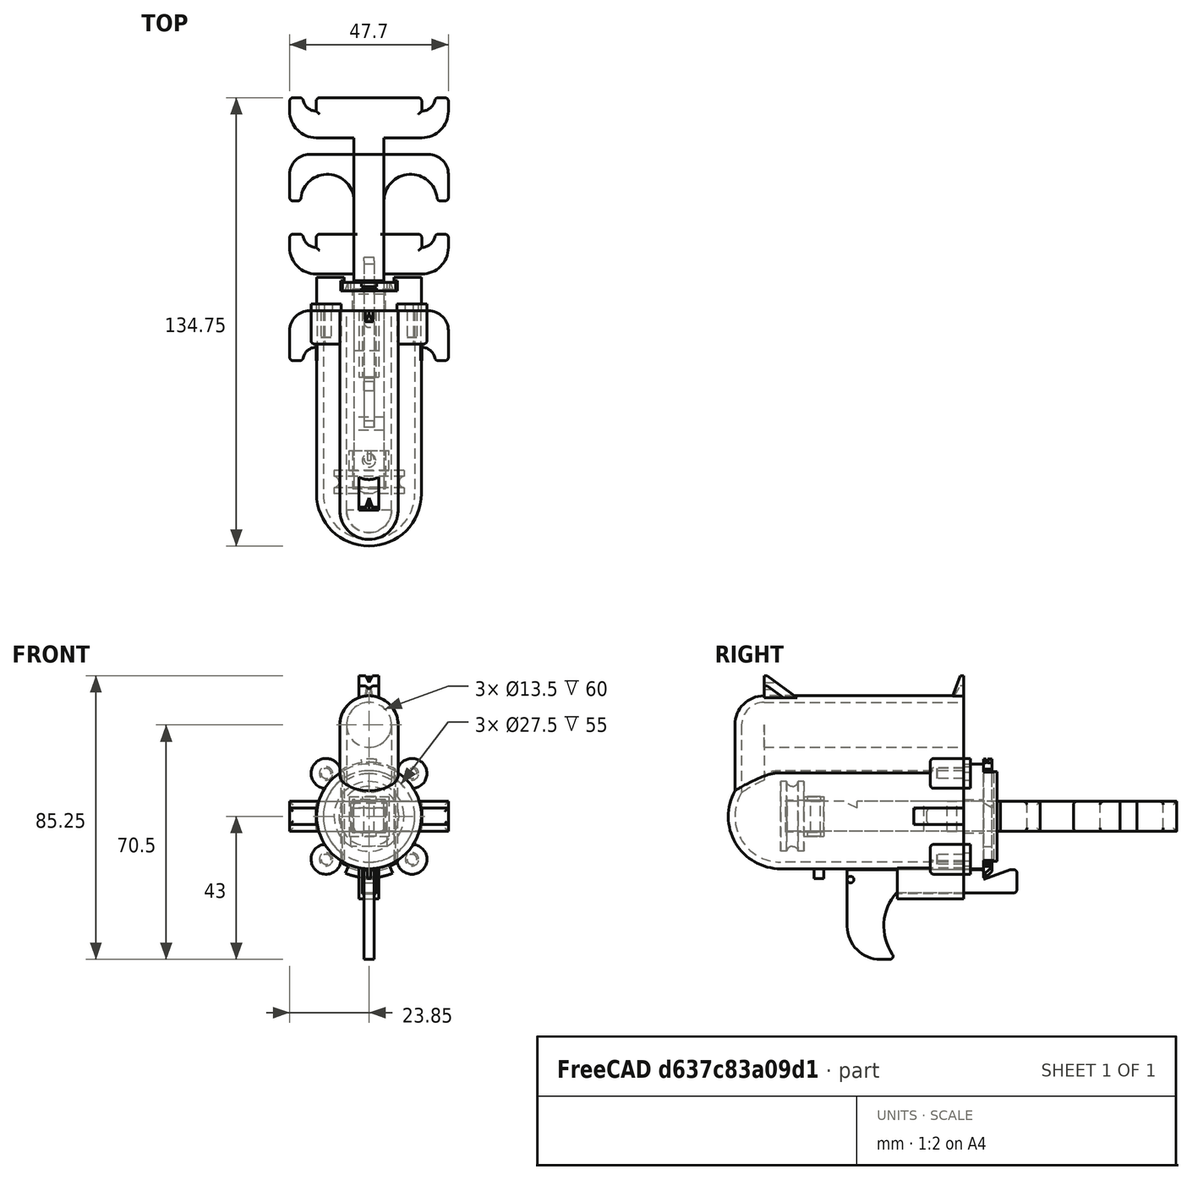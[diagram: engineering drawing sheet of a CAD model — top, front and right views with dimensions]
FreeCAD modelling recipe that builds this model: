
FCSTD DOCUMENT  (FreeCAD 0.19R24267 +99 (Git))
Label: miniU
License: All rights reserved
LicenseURL: http://en.wikipedia.org/wiki/All_rights_reserved
objects: PartDesign::SubtractiveCylinder×25, PartDesign::AdditiveCylinder×21, PartDesign::AdditiveBox×18, PartDesign::Fillet×15, PartDesign::Mirrored×10, PartDesign::Body×10, PartDesign::AdditiveSphere×8, PartDesign::PolarPattern×8, PartDesign::SubtractiveBox×8, PartDesign::SubtractiveSphere×6, PartDesign::SubtractiveWedge×5, PartDesign::AdditiveWedge×5, Sketcher::SketchObject×1, PartDesign::SubtractiveTorus×1, PartDesign::Chamfer×1
note: 255 computed .brp shape members not serialized (recipe doc carries the construction recipe); baked Part::Feature solids carry a one-line shape summary decoded from their .brp

FEATURE [PartDesign::AdditiveCylinder] Cylinder001  label="dart_holder_body"
  Angle = 360
  AttacherType = Attacher::AttachEngine3D
  AttachmentOffset = pos=(0,27.5,0) rot=(0,0,1;0rad)
  Height = 60
  MapMode = 5
  Placement = pos=(0,-6.1e-15,27.5) rot=(1,0,0;1.5708rad)
  Radius = 8.75
  Support = -> [XZ_Plane]
  expr: .AttachmentOffset.Base.y = Sketch.Constraints.chamberToHolder
  expr: Radius = Sketch.Constraints.rDartHolderOutside
  expr: Height = Sketch.Constraints.bodyLength + Sketch.Constraints.holderOffset
FEATURE [PartDesign::AdditiveBox] Box  label="chamber_holder_connector"
  AttacherType = Attacher::AttachEngine3D
  AttachmentOffset = pos=(-8.75,0,-60) rot=(0,0,1;0rad)
  BaseFeature = -> Cylinder001
  Height = 60
  Length = 17.5
  MapMode = 5
  Placement = pos=(-8.75,-60,27.5) rot=(-1,0,0;1.5708rad)
  Support = -> [Cylinder001]
  Width = 27.5
  expr: Length = Cylinder001.Radius * 2
  expr: .AttachmentOffset.Base.x = -Cylinder001.Radius
  expr: .AttachmentOffset.Base.z = -Cylinder001.Height
  expr: Height = Cylinder001.Height
  expr: Width = Sketch.Constraints.chamberToHolder
FEATURE [PartDesign::AdditiveSphere] Sphere  label="chamber_butt"
  Angle1 = -90
  Angle2 = 90
  Angle3 = 180
  AttacherType = Attacher::AttachEngine3D
  AttachmentOffset = pos=(-8.75,5,0) rot=(0,0,-1;3.14159rad)
  BaseFeature = -> Box
  MapMode = 5
  Placement = pos=(0,-55,-1.31e-14) rot=(-1,0,0;3.14159rad)
  Radius = 15.75
  Support = -> [Box]
  expr: .AttachmentOffset.Base.y = Sketch.Constraints.holderOffset
  expr: .AttachmentOffset.Base.x = -Cylinder001.Radius
  expr: Radius = Sketch.Constraints.rAirChamberOutside
FEATURE [PartDesign::AdditiveSphere] Sphere002  label="holder_butt"
  Angle1 = -90
  Angle2 = 90
  Angle3 = 360
  AttacherType = Attacher::AttachEngine3D
  BaseFeature = -> Sphere
  MapMode = 11
  Placement = pos=(0,-60,27.5) rot=(0.57735,-0.57735,0.57735;2.0944rad)
  Radius = 8.75
  Support = -> [Cylinder001]
  expr: Radius = Cylinder001.Radius
FEATURE [PartDesign::AdditiveCylinder] Cylinder  label="butt_connector"
  Angle = 180
  AttacherType = Attacher::AttachEngine3D
  AttachmentOffset = pos=(-8.75,0,-27.5) rot=(0,0,1;3.14159rad)
  BaseFeature = -> Sphere002
  Height = 27.5
  MapMode = 5
  Placement = pos=(0,-60,27.5) rot=(1,0,0;3.14159rad)
  Radius = 8.75
  Support = -> [Box]
  expr: .AttachmentOffset.Base.x = -Radius
  expr: Radius = Sphere002.Radius
  expr: Height = Box.Width
  expr: .AttachmentOffset.Base.z = -Box.Width
FEATURE [Sketcher::SketchObject] Sketch
  FullyConstrained = false
  MapMode = 5
  Placement = pos=(0,0,0) rot=(1,0,0;1.5708rad)
  expr: .Constraints.rAirChamber = 13.75mm
  expr: .Constraints.rDartHolderOutside = .Constraints.rDartHolder + .Constraints.wallThickness
  expr: .Constraints.chamberToHolder = .Constraints.rAirChamberOutside + .Constraints.rDartHolderOutside + .Constraints.triggerClearance
  expr: .Constraints.plungerHeadSpace = .Constraints.plungerHeadHeight + .Constraints.plungerConnectorHeight + 7mm
  sketch-geometry (40):
    g0: Circle CenterX=0 CenterY=0 CenterZ=0 NormalX=0 NormalY=0 NormalZ=1 AngleXU=0 Radius=13.75
    g1: Circle CenterX=0 CenterY=0 CenterZ=0 NormalX=0 NormalY=0 NormalZ=1 AngleXU=0 Radius=15.75
    g2: LineSegment StartX=0 StartY=0 StartZ=0 EndX=-11.1369 EndY=11.1369 EndZ=0
    g3: LineSegment StartX=0 StartY=0 StartZ=0 EndX=11.1369 EndY=-11.1369 EndZ=0
    g4: LineSegment StartX=0 StartY=0 StartZ=0 EndX=-11.1369 EndY=-11.1369 EndZ=0
    g5: LineSegment StartX=0 StartY=0 StartZ=0 EndX=11.1369 EndY=11.1369 EndZ=0
    g6: Circle CenterX=-12.9047 CenterY=12.9047 CenterZ=0 NormalX=0 NormalY=0 NormalZ=1 AngleXU=0 Radius=4.5
    g7: Circle CenterX=-12.9047 CenterY=12.9047 CenterZ=0 NormalX=0 NormalY=0 NormalZ=1 AngleXU=0 Radius=1.5
    g8: Circle CenterX=12.9047 CenterY=12.9047 CenterZ=0 NormalX=0 NormalY=0 NormalZ=1 AngleXU=0 Radius=4.5
    g9: Circle CenterX=12.9047 CenterY=-12.9047 CenterZ=0 NormalX=0 NormalY=0 NormalZ=1 AngleXU=0 Radius=4.5
    g10: Circle CenterX=-12.9047 CenterY=-12.9047 CenterZ=0 NormalX=0 NormalY=0 NormalZ=1 AngleXU=0 Radius=4.5
    g11: Circle CenterX=12.9047 CenterY=12.9047 CenterZ=0 NormalX=0 NormalY=0 NormalZ=1 AngleXU=0 Radius=2.5
    g12: Circle CenterX=12.9047 CenterY=-12.9047 CenterZ=0 NormalX=0 NormalY=0 NormalZ=1 AngleXU=0 Radius=2.5
    g13: Circle CenterX=-12.9047 CenterY=-12.9047 CenterZ=0 NormalX=0 NormalY=0 NormalZ=1 AngleXU=0 Radius=2.5
    g14: LineSegment StartX=-64.4343 StartY=16.9456 StartZ=0 EndX=-65.991 EndY=15.6899 EndZ=0
    g15: Circle CenterX=0 CenterY=27.5 CenterZ=0 NormalX=0 NormalY=0 NormalZ=1 AngleXU=0 Radius=6.75
    g16: Circle CenterX=0 CenterY=27.5 CenterZ=0 NormalX=0 NormalY=0 NormalZ=1 AngleXU=0 Radius=8.75
    g17: LineSegment StartX=-40.3343 StartY=20.9092 StartZ=0 EndX=-43.3342 EndY=20.8833 EndZ=0
    g18: LineSegment StartX=-25.2142 StartY=68.5251 StartZ=0 EndX=-61.5111 EndY=27.2028 EndZ=0
    g19: LineSegment StartX=21.11 StartY=51.0184 StartZ=0 EndX=24.006 EndY=46.9425 EndZ=0
    g20: LineSegment StartX=-12.7279 StartY=-12.7279 StartZ=0 EndX=12.7279 EndY=-12.7279 EndZ=0
    g21: LineSegment StartX=52.0801 StartY=33.9087 StartZ=0 EndX=59.1988 EndY=26.8856 EndZ=0
    g22: LineSegment StartX=35.6743 StartY=43.6176 StartZ=0 EndX=37.6673 EndY=43.4507 EndZ=0
    g23: Circle CenterX=-12.9047 CenterY=12.9047 CenterZ=0 NormalX=0 NormalY=0 NormalZ=1 AngleXU=0 Radius=2
    g24: LineSegment StartX=-26.9818 StartY=14.1414 StartZ=0 EndX=-26.9818 EndY=4.14137 EndZ=0
    g25: LineSegment StartX=-27.1419 StartY=18.6048 StartZ=0 EndX=-17.1419 EndY=18.6048 EndZ=0
    g26: LineSegment StartX=97.724 StartY=55.6573 StartZ=0 EndX=98.9263 EndY=52.9088 EndZ=0
    g27: LineSegment StartX=114.207 StartY=50.7764 StartZ=0 EndX=114.698 EndY=50.6847 EndZ=0
    g28: LineSegment StartX=128.072 StartY=57.8158 StartZ=0 EndX=130.022 EndY=55.5362 EndZ=0
    g29: LineSegment StartX=-62.4879 StartY=52.9152 StartZ=0 EndX=-78.8492 EndY=39.7505 EndZ=0
    g30: LineSegment StartX=-15.7414 StartY=69.7309 StartZ=0 EndX=44.2586 EndY=69.7309 EndZ=0
    g31: Circle CenterX=50.0754 CenterY=-16.528 CenterZ=0 NormalX=0 NormalY=0 NormalZ=1 AngleXU=0 Radius=9.625
    g32: LineSegment StartX=83.804 StartY=28.6893 StartZ=0 EndX=88.0476 EndY=23.1224 EndZ=0
    g33: LineSegment StartX=90.4529 StartY=40.1785 StartZ=0 EndX=95.8588 EndY=35.7314 EndZ=0
    g34: Circle CenterX=93.0757 CenterY=-11.2423 CenterZ=0 NormalX=0 NormalY=0 NormalZ=1 AngleXU=0 Radius=9.25
    g35: Circle CenterX=102.66 CenterY=-16.1107 CenterZ=0 NormalX=0 NormalY=0 NormalZ=1 AngleXU=0 Radius=1.5
    g36: LineSegment StartX=-47.4906 StartY=-5.12483 StartZ=0 EndX=-47.4906 EndY=-8.12483 EndZ=0
    g37: LineSegment StartX=-47.4906 StartY=-8.12483 StartZ=0 EndX=-40.4906 EndY=-8.12483 EndZ=0
    g38: LineSegment StartX=-97.7001 StartY=1.7101 StartZ=0 EndX=-97.7001 EndY=-14.2899 EndZ=0
    g39: LineSegment StartX=-37.3838 StartY=-26.4694 StartZ=0 EndX=-35.296 EndY=-32.0944 EndZ=0
  constraints (78):
    c: Coincident(g0,g-1)
    c: Coincident(g1,g0)
    c: Radius(g0) = 13.75  'rAirChamber'
    c: Radius(g1) = 15.75  'rAirChamberOutside'
    c: Coincident(g2,g0)
    c: PointOnObject(g2,g1)
    c: Coincident(g3,g0)
    c: PointOnObject(g3,g1)
    c: Coincident(g4,g0)
    c: PointOnObject(g4,g1)
    c: Angle(g2) = 2.35619
    c: Angle(g3) = -0.785398
    c: Angle(g4) = -2.35619
    c: Coincident(g5,g0)
    c: PointOnObject(g5,g1)
    c: Angle(g5) = 0.785398
    c: PointOnObject(g6,g2)
    c: Diameter(g6) = 9  'dNutOutside'
    c: Coincident(g7,g6)
    c: Diameter(g7) = 3  'dInsert'
    c: Equal(g8,g10)
    c: PointOnObject(g8,g5)
    c: PointOnObject(g9,g3)
    c: PointOnObject(g10,g4)
    c: Coincident(g11,g8)
    c: Coincident(g12,g9)
    c: Coincident(g13,g10)
    c: Equal(g11,g12)
    c: Distance(g14) = 2  'wallThickness'
    c: PointOnObject(g15,g-2)
    c: Coincident(g16,g15)
    c: Radius(g15) = 6.75  'rDartHolder'
    c: Radius(g16) = 8.75  'rDartHolderOutside'
    c: Distance(g15,g0) = 27.5  'chamberToHolder'
    c: Distance(g17) = 3  'triggerClearance'
    c: Distance(g18) = 55  'bodyLength'
    c: Tangent(g6,g0)
    c: Tangent(g8,g0)
    c: Tangent(g9,g0)
    c: Tangent(g10,g0)
    c: Distance(g19) = 5  'holderOffset'
    c: Distance(g20) = 25.4558  'threadDistance'
    c: Distance(g21) = 10  'chamberCapThickness'
    c: Radius(g6) = 4.5  'rNutOutside'
    c: Radius(g7) = 1.5  'rInsert'
    c: Distance(g22) = 2  'capThreadThickness'
    c: Coincident(g23,g6)
    c: Radius(g23) = 2  'rThread'
    c: Vertical(g24)
    c: Horizontal(g25)
    c: Distance(g25) = 10  'capHoleWidth'
    c: Distance(g24) = 10  'capHoleLength'
    c: Equal(g6,g8)
    c: Equal(g8,g9)
    c: Equal(g12,g13)
    c: Distance(g26) = 3  'triggerFrame'
    c: Distance(g27) = 0.5  'triggerFrameClearance'
    c: Distance(g28) = 3  'triggerFrameThickness'
    c: Distance(g29) = 21  'plungerHeadSpace'
    c: Horizontal(g30)
    c: Distance(g30) = 60  'plungerLength'
    c: Diameter(g31) = 19.25  'dPlungerHead'
    c: Radius(g31) = 9.625  'rPlungerHead'
    c: Distance(g32) = 7  'plungerHeadHeight'
    c: Distance(g33) = 7  'plungerConnectorHeight'
    c: Tangent(g35,g34)
    c: Diameter(g34) = 18.5  'oRingD1'
    c: Diameter(g35) = 3  'oRingD2'
    c: Radius(g34) = 9.25  'oRingR1'
    c: Radius(g35) = 1.5  'oRingR2'
    c: Vertical(g36)
    c: Coincident(g37,g36)
    c: Horizontal(g37)
    c: Distance(g36) = 3  'triggerPullerWidth'
    c: Distance(g37) = 7  'triggerPullerLength'
    c: Vertical(g38)
    c: Distance(g38) = 16  'pullerSpacing'
    c: Distance(g39) = 6  'sightHeight'
FEATURE [PartDesign::AdditiveCylinder] Cylinder002  label="air_chamber_body"
  Angle = 360
  AttacherType = Attacher::AttachEngine3D
  BaseFeature = -> Cylinder
  Height = 55
  MapMode = 2
  Placement = pos=(0,0,0) rot=(1,0,0;1.5708rad)
  Radius = 15.75
  Support = -> [Sketch]
  expr: Radius = Sketch.Constraints.rAirChamberOutside
  expr: Height = Sketch.Constraints.bodyLength
FEATURE [PartDesign::SubtractiveCylinder] Cylinder003  label="air_chamber"
  Angle = 360
  AttacherType = Attacher::AttachEngine3D
  BaseFeature = -> Cylinder002
  Height = 55
  MapMode = 2
  Placement = pos=(0,0,0) rot=(1,0,0;1.5708rad)
  Radius = 13.75
  Support = -> [Sketch]
  expr: Radius = Sketch.Constraints.rAirChamber
  expr: Height = Cylinder001.Height - Sketch.Constraints.holderOffset
FEATURE [PartDesign::SubtractiveCylinder] Cylinder004  label="butt_connector_channel"
  Angle = 180
  AttacherType = Attacher::AttachEngine3D
  BaseFeature = -> Cylinder003
  Height = 27.5
  MapMode = 2
  Placement = pos=(0,-60,27.5) rot=(1,0,0;3.14159rad)
  Radius = 6.75
  Support = -> [Cylinder]
  expr: Radius = Cylinder.Radius - 2mm
  expr: Height = Cylinder.Height
FEATURE [PartDesign::SubtractiveSphere] Sphere003
  Angle1 = -90
  Angle2 = 90
  Angle3 = 180
  AttacherType = Attacher::AttachEngine3D
  BaseFeature = -> Cylinder004
  MapMode = 2
  Placement = pos=(0,-55,-1.31e-14) rot=(1,0,0;3.14159rad)
  Radius = 13.75
  Support = -> [Sphere]
  expr: Radius = Sketch.Constraints.rAirChamber
FEATURE [PartDesign::SubtractiveCylinder] Cylinder005  label="dart_holder"
  Angle = 360
  AttacherType = Attacher::AttachEngine3D
  AttachmentOffset = pos=(0,0,-60) rot=(0,0,1;0rad)
  BaseFeature = -> Sphere003
  Height = 60
  MapMode = 5
  Placement = pos=(0,-60,27.5) rot=(-1,0,0;1.5708rad)
  Radius = 6.75
  Support = -> [Cylinder001]
  expr: Radius = Cylinder001.Radius - 2mm
  expr: Height = Cylinder001.Height
  expr: .AttachmentOffset.Base.z = -Cylinder001.Height
FEATURE [PartDesign::SubtractiveSphere] Sphere004
  Angle1 = -90
  Angle2 = 90
  Angle3 = 360
  AttacherType = Attacher::AttachEngine3D
  BaseFeature = -> Cylinder005
  MapMode = 2
  Placement = pos=(0,-60,27.5) rot=(-0.57735,0.57735,-0.57735;4.18879rad)
  Radius = 6.75
  Support = -> [Sphere002]
  expr: Radius = Sphere002.Radius - 2mm
FEATURE [PartDesign::AdditiveCylinder] Cylinder006
  Angle = 360
  AttacherType = Attacher::AttachEngine3D
  BaseFeature = -> Sphere004
  Height = 10
  MapMode = 11
  Placement = pos=(-12.9047,2.9e-15,12.9047) rot=(0.57735,-0.57735,0.57735;2.0944rad)
  Radius = 4.5
  Support = -> [Sketch]
  expr: Radius = Sketch.Constraints.dNutOutside / 2
FEATURE [PartDesign::PolarPattern] PolarPattern
  Angle = 360
  Axis = -> Y_Axis
  BaseFeature = -> Cylinder006
  Occurrences = 4
  Originals = -> [Cylinder006]
  Placement = pos=(-12.9047,3e-15,12.9047) rot=(0.57735,-0.57735,0.57735;2.0944rad)
FEATURE [PartDesign::SubtractiveCylinder] Cylinder007
  Angle = 360
  AttacherType = Attacher::AttachEngine3D
  BaseFeature = -> PolarPattern
  Height = 8
  MapMode = 11
  Placement = pos=(-12.9047,2.9e-15,12.9047) rot=(0.57735,-0.57735,0.57735;2.0944rad)
  Radius = 1.5
  Support = -> [Sketch]
  expr: Radius = Sketch.Constraints.dInsert / 2
  expr: Height = Cylinder006.Height - 2mm
FEATURE [PartDesign::AdditiveCylinder] Cylinder008  label="cap_body"
  Angle = 360
  AttacherType = Attacher::AttachEngine3D
  AttachmentOffset = pos=(0,0,0) rot=(0,1,0;3.14159rad)
  Height = 10
  MapMode = 5
  Placement = pos=(0,0,0) rot=(0,0.707107,0.707107;3.14159rad)
  Radius = 15.75
  Refine = true
  Support = -> [XZ_Plane001]
  expr: Radius = Sketch.Constraints.rAirChamberOutside
  expr: Height = Sketch.Constraints.chamberCapThickness
FEATURE [PartDesign::AdditiveCylinder] Cylinder009
  Angle = 360
  AttacherType = Attacher::AttachEngine3D
  AttachmentOffset = pos=(0,0,0) rot=(0,1,0;3.14159rad)
  BaseFeature = -> Cylinder008
  Height = 2
  MapMode = 11
  Placement = pos=(12.9047,-2.9e-15,-12.9047) rot=(-0.57735,0.57735,0.57735;2.0944rad)
  Radius = 4.5
  Refine = true
  Support = -> [Sketch]
  expr: Height = Sketch.Constraints.capThreadThickness
  expr: Radius = Sketch.Constraints.rNutOutside
FEATURE [PartDesign::PolarPattern] PolarPattern002
  Angle = 360
  Axis = -> Y_Axis001
  BaseFeature = -> Cylinder009
  Occurrences = 4
  Originals = -> [Cylinder009]
  Placement = pos=(12.9047,-3e-15,-12.9047) rot=(0.57735,-0.57735,-0.57735;4.18879rad)
  Refine = true
FEATURE [PartDesign::SubtractiveCylinder] Cylinder010
  Angle = 360
  AttacherType = Attacher::AttachEngine3D
  AttachmentOffset = pos=(0,0,0) rot=(0,1,0;3.14159rad)
  BaseFeature = -> PolarPattern002
  Height = 2
  MapMode = 11
  Placement = pos=(12.9047,2.9e-15,12.9047) rot=(-0.57735,0.57735,0.57735;2.0944rad)
  Radius = 2
  Refine = true
  Support = -> [Sketch]
  expr: Radius = Sketch.Constraints.rThread
  expr: Height = Cylinder009.Height
FEATURE [PartDesign::PolarPattern] PolarPattern003
  Angle = 360
  Axis = -> Y_Axis001
  BaseFeature = -> Cylinder010
  Occurrences = 4
  Originals = -> [Cylinder010]
  Placement = pos=(12.9047,3e-15,12.9047) rot=(0.57735,-0.57735,-0.57735;4.18879rad)
  Refine = true
FEATURE [PartDesign::PolarPattern] PolarPattern001
  Angle = 360
  Axis = -> Y_Axis
  BaseFeature = -> Cylinder007
  Occurrences = 4
  Originals = -> [Cylinder007]
  Placement = pos=(-12.9047,3e-15,12.9047) rot=(0.57735,-0.57735,0.57735;2.0944rad)
FEATURE [PartDesign::SubtractiveBox] Box001  label="cap_hole"
  AttacherType = Attacher::AttachEngine3D
  AttachmentOffset = pos=(5,-5,0) rot=(0,1,0;3.14159rad)
  BaseFeature = -> PolarPattern003
  Height = 10
  Length = 10
  MapMode = 5
  Placement = pos=(5,1.1e-15,-5) rot=(0,0.707107,0.707107;3.14159rad)
  Refine = true
  Support = -> [XZ_Plane001]
  Width = 10
  expr: Height = Cylinder008.Height
  expr: Width = Sketch.Constraints.capHoleWidth
  expr: Length = Sketch.Constraints.capHoleLength
  expr: .AttachmentOffset.Base.y = -Width / 2
  expr: .AttachmentOffset.Base.x = Length / 2
FEATURE [PartDesign::AdditiveBox] Box002  label="plungerBody"
  AttacherType = Attacher::AttachEngine3D
  AttachmentOffset = pos=(-4.5,-4.5,0) rot=(0,0,1;0rad)
  Height = 64
  Length = 9
  MapMode = 5
  Placement = pos=(-4.5,1e-15,-4.5) rot=(1,0,0;1.5708rad)
  Refine = true
  Support = -> [XZ_Plane003]
  Width = 9
  expr: .AttachmentOffset.Base.x = -Length / 2
  expr: .AttachmentOffset.Base.y = -Width / 2
  expr: Length = Sketch.Constraints.capHoleLength - 1mm
  expr: Width = Sketch.Constraints.capHoleWidth - 1mm
  expr: Height = Sketch.Constraints.bodyLength + 9mm
FEATURE [PartDesign::SubtractiveWedge] Wedge
  AttacherType = Attacher::AttachEngine3D
  AttachmentOffset = pos=(-9,43,-2) rot=(0,0,1;0rad)
  BaseFeature = -> Box002
  MapMode = 5
  Placement = pos=(4.5,-43,2.5) rot=(0,0,1;3.14159rad)
  Refine = true
  Support = -> [Box002]
  X2max = 9
  X2min = 0
  Xmax = 9
  Xmin = 0
  Ymax = 4
  Ymin = 0
  Z2max = 2
  Z2min = 2
  Zmax = 2
  Zmin = 0
  expr: X2max = Xmax
  expr: Xmax = <<plungerBody>>.Length
  expr: .AttachmentOffset.Base.y = Box002.Height - Sketch.Constraints.plungerHeadSpace
  expr: .AttachmentOffset.Base.x = -Xmax / 2 - Box002.Length / 2
FEATURE [PartDesign::SubtractiveBox] Box003  label="trigger_housing"
  AttacherType = Attacher::AttachEngine3D
  AttachmentOffset = pos=(16.25,-8.5,-1) rot=(0,1,0;3.14159rad)
  BaseFeature = -> Box001
  Height = 3.1
  Length = 32.5
  MapMode = 11
  Placement = pos=(-8.5,9,16.25) rot=(0.57735,0.57735,-0.57735;2.0944rad)
  Refine = true
  Support = -> [Box001]
  Width = 17
  expr: .AttachmentOffset.Base.z = -Sketch.Constraints.wallThickness / 2
  expr: Height = Sketch.Constraints.triggerFrameThickness + 0.1mm
  expr: Width = Box001.Length + Sketch.Constraints.triggerFrame * 2 + Sketch.Constraints.triggerFrameClearance * 2
  expr: Length = Cylinder008.Radius * 2 + 1mm
  expr: .AttachmentOffset.Base.y = -Width / 2
  expr: .AttachmentOffset.Base.x = Length / 2
FEATURE [PartDesign::SubtractiveBox] Box004  label="cap_cutout"
  AttacherType = Attacher::AttachEngine3D
  AttachmentOffset = pos=(16.25,-7.5,0) rot=(0,1,0;3.14159rad)
  BaseFeature = -> Box003
  Height = 1
  Length = 32.5
  MapMode = 11
  Placement = pos=(-7.5,10,16.25) rot=(-0.57735,-0.57735,0.57735;4.18879rad)
  Refine = true
  Support = -> [Box003]
  Width = 15
  expr: Height = Sketch.Constraints.wallThickness / 2
  expr: Width = <<trigger_housing>>.Width - 2mm
  expr: .AttachmentOffset.Base.y = -Width / 2
  expr: .AttachmentOffset.Base.x = Length / 2
  expr: Length = <<trigger_housing>>.Length
FEATURE [PartDesign::AdditiveCylinder] Cylinder013
  Angle = 15
  AttacherType = Attacher::AttachEngine3D
  AttachmentOffset = pos=(0,0,2.5) rot=(0.659346,0.75184,0;3.14159rad)
  Height = 2.5
  MapMode = 5
  Placement = pos=(0,-2.5,-6e-16) rot=(0.527011,0.600941,0.600941;4.11164rad)
  Radius = 17.25
  Refine = true
  Support = -> [XZ_Plane002]
  expr: Radius = Cylinder008.Radius + 1.5mm
  expr: .AttachmentOffset.Rotation.Yaw = 90° + Angle / 2
  expr: .AttachmentOffset.Base.z = Sketch.Constraints.triggerFrameThickness - 0.5mm
FEATURE [PartDesign::SubtractiveBox] Box007
  AttacherType = Attacher::AttachEngine3D
  AttachmentOffset = pos=(0,3,1) rot=(1,0,0;3.14159rad)
  BaseFeature = -> Cylinder013
  Height = 3
  Length = 0.5
  MapMode = 45
  Placement = pos=(-3,-1.25,18.2008) rot=(0.707107,0.707107,0;3.14159rad)
  Refine = true
  Support = -> [Cylinder013]
  Width = 6
FEATURE [PartDesign::AdditiveCylinder] Cylinder011
  Angle = 360
  AttacherType = Attacher::AttachEngine3D
  BaseFeature = -> Box007
  Height = 2.5
  MapMode = 2
  Placement = pos=(0,0,0) rot=(1,0,0;1.5708rad)
  Radius = 16.25
  Refine = true
  Support = -> [XZ_Plane002]
  expr: Height = Sketch.Constraints.triggerFrameThickness - 0.5mm
  expr: Radius = Cylinder008.Radius + 0.5mm
FEATURE [PartDesign::AdditiveCylinder] Cylinder012
  Angle = 45
  AttacherType = Attacher::AttachEngine3D
  AttachmentOffset = pos=(0,0,0) rot=(0,0,-1;1.96349rad)
  BaseFeature = -> Cylinder011
  Height = 2.5
  MapMode = 5
  Placement = pos=(0,0,0) rot=(0.427192,0.639338,-0.639338;2.33414rad)
  Radius = 18.5
  Refine = true
  Support = -> [XZ_Plane002]
  expr: Height = Cylinder011.Height
  expr: .AttachmentOffset.Rotation.Yaw = -90deg - Angle / 2
FEATURE [PartDesign::SubtractiveCylinder] Cylinder014
  Angle = 360
  AttacherType = Attacher::AttachEngine3D
  AttachmentOffset = pos=(0,0,0) rot=(1,0,0;3.14159rad)
  BaseFeature = -> Cylinder012
  Height = 10
  MapMode = 5
  Placement = pos=(0,0,0) rot=(1,0,0;4.71239rad)
  Radius = 16.25
  Refine = true
  Support = -> [XZ_Plane002]
  expr: Radius = <<air_chamber_body>>.Radius + 0.5mm
FEATURE [PartDesign::SubtractiveBox] Box005
  AttacherType = Attacher::AttachEngine3D
  AttachmentOffset = pos=(-5.5,-9,0) rot=(0,0,1;0rad)
  BaseFeature = -> Cylinder014
  Height = 2.5
  Length = 11
  MapMode = 5
  Placement = pos=(-5.5,2e-15,-9) rot=(1,0,0;1.5708rad)
  Refine = true
  Support = -> [XZ_Plane002]
  Width = 14
  expr: Length = <<cap_hole>>.Length + 1mm
  expr: .AttachmentOffset.Base.x = -Length / 2
  expr: Width = <<cap_hole>>.Width + 4mm
  expr: .AttachmentOffset.Base.y = -Width / 2 - 2mm
  expr: Height = Cylinder011.Height
FEATURE [PartDesign::AdditiveWedge] Wedge001
  AttacherType = Attacher::AttachEngine3D
  AttachmentOffset = pos=(11,3,0) rot=(0,0,1;3.14159rad)
  BaseFeature = -> Box005
  MapMode = 5
  Placement = pos=(5.5,-3,5) rot=(0,-1,0;3.14159rad)
  Refine = true
  Support = -> [Box005]
  X2max = 11
  X2min = 0
  Xmax = 11
  Xmin = 0
  Ymax = 3
  Ymin = 0.5
  Z2max = 1
  Z2min = 0
  Zmax = 2.5
  Zmin = 0
  expr: X2max = Box005.Length
  expr: Xmax = Box005.Length
FEATURE [PartDesign::SubtractiveBox] Box006
  AttacherType = Attacher::AttachEngine3D
  AttachmentOffset = pos=(8,-16.25,0) rot=(0,0,1;0rad)
  BaseFeature = -> Wedge001
  Height = 10
  Length = 11
  MapMode = 5
  Placement = pos=(8,3.6e-15,-16.25) rot=(1,0,0;1.5708rad)
  Refine = true
  Support = -> [XZ_Plane002]
  Width = 32.5
  expr: Width = Cylinder011.Radius * 2
  expr: .AttachmentOffset.Base.y = -Width / 2
  expr: .AttachmentOffset.Base.x = <<trigger_housing>>.Width / 2 - 0.5mm
FEATURE [PartDesign::Mirrored] Mirrored
  BaseFeature = -> Box006
  MirrorPlane = -> YZ_Plane002
  Originals = -> [Box006]
  Placement = pos=(8,4e-15,-16.25) rot=(1,0,0;1.5708rad)
  Refine = true
FEATURE [PartDesign::Fillet] Fillet005
  Base = -> Box004 [Edge16,Edge8,Edge2,Edge10]
  BaseFeature = -> Box004
  Placement = pos=(-7.5,10,16.25) rot=(0.57735,0.57735,-0.57735;2.0944rad)
  Radius = 0.5
  Refine = true
  SupportTransform = false
FEATURE [PartDesign::Body] Body001  label="cap"
  Group = -> [Cylinder008,Cylinder009,PolarPattern002,Cylinder010,PolarPattern003,Box001,Box003,Box004,Fillet005]
  Origin = -> Origin001
  Tip = -> Fillet005
FEATURE [PartDesign::AdditiveCylinder] Cylinder019  label="oRingHolder"
  Angle = 360
  AttacherType = Attacher::AttachEngine3D
  Height = 7
  MapMode = 5
  Placement = pos=(0,0,0) rot=(1,0,0;1.5708rad)
  Radius = 10.5
  Refine = true
  Support = -> [XZ_Plane004]
  expr: Radius = Sketch.Constraints.oRingR1 + Sketch.Constraints.oRingR2 - 0.25mm
  expr: Height = Sketch.Constraints.plungerHeadHeight
FEATURE [PartDesign::AdditiveBox] Box016  label="plungerConnector"
  AttacherType = Attacher::AttachEngine3D
  AttachmentOffset = pos=(-6,-6,0) rot=(0,0,1;0rad)
  BaseFeature = -> Cylinder019
  Height = 6
  Length = 12
  MapMode = 5
  Placement = pos=(-6,-1.3e-15,6) rot=(-1,0,0;1.5708rad)
  Refine = true
  Support = -> [Cylinder019]
  Width = 12
  expr: .AttachmentOffset.Base.x = -Length / 2
  expr: .AttachmentOffset.Base.y = -Width / 2
  expr: Length = <<plungerBody>>.Length + Sketch.Constraints.wallThickness + 1mm
  expr: Width = <<plungerBody>>.Width + Sketch.Constraints.wallThickness + 1mm
  expr: Height = Sketch.Constraints.rThread * 2 + Sketch.Constraints.wallThickness
FEATURE [PartDesign::SubtractiveBox] Box017  label="plungerFitHole"
  AttacherType = Attacher::AttachEngine3D
  AttachmentOffset = pos=(-5,-4.75,-6) rot=(0,0,1;0rad)
  BaseFeature = -> Box016
  Height = 11.5
  Length = 10
  MapMode = 5
  Placement = pos=(-5,6,-4.75) rot=(1,0,0;1.5708rad)
  Refine = true
  Support = -> [XZ_Plane004]
  Width = 9.5
  expr: .AttachmentOffset.Base.y = -Width / 2
  expr: .AttachmentOffset.Base.x = -Length / 2
  expr: .AttachmentOffset.Base.z = -Box016.Height
  expr: Height = Box016.Height + Cylinder019.Height - Sketch.Constraints.wallThickness + 0.5mm
  expr: Length = <<plungerBody>>.Length + 1mm
  expr: Width = <<plungerBody>>.Width + 0.5mm
FEATURE [PartDesign::SubtractiveCylinder] Cylinder020  label="plungerHeadNutHole"
  Angle = 360
  AttacherType = Attacher::AttachEngine3D
  AttachmentOffset = pos=(0,3,6) rot=(1,0,0;3.14159rad)
  BaseFeature = -> Box017
  Height = 12
  MapMode = 5
  Placement = pos=(0,3,6) rot=(1,0,0;3.14159rad)
  Radius = 2
  Refine = true
  Support = -> [XY_Plane004]
  expr: .AttachmentOffset.Base.y = Radius + 1mm
  expr: Radius = Sketch.Constraints.rThread
  expr: Height = <<plungerConnector>>.Width
  expr: .AttachmentOffset.Base.z = <<plungerConnector>>.Width / 2
FEATURE [PartDesign::SubtractiveCylinder] Cylinder021
  Angle = 360
  AttacherType = Attacher::AttachEngine3D
  AttachmentOffset = pos=(0,-55.5,-4.5) rot=(0,0,1;0rad)
  BaseFeature = -> Wedge
  Height = 9
  MapMode = 5
  Placement = pos=(0,-55.5,-4.5) rot=(0,0,1;0rad)
  Radius = 1.5
  Refine = true
  Support = -> [XY_Plane003]
  expr: .AttachmentOffset.Base.y = -<<plungerBody>>.Height + Box017.Height - <<plungerConnector>>.Height / 2
  expr: .AttachmentOffset.Base.z = -<<plungerBody>>.Width / 2
  expr: Radius = Sketch.Constraints.rInsert
  expr: Height = <<plungerBody>>.Width
FEATURE [PartDesign::SubtractiveTorus] Torus  label="oRingFit"
  Angle1 = -180
  Angle2 = 180
  Angle3 = 360
  AttacherType = Attacher::AttachEngine3D
  AttachmentOffset = pos=(0,0,3.5) rot=(0,0,1;0rad)
  BaseFeature = -> Cylinder020
  MapMode = 5
  Placement = pos=(0,-3.5,-8e-16) rot=(1,0,0;1.5708rad)
  Radius1 = 10.75
  Radius2 = 1.75
  Refine = true
  Support = -> [XZ_Plane004]
  expr: Radius2 = Sketch.Constraints.oRingR2 + 0.25mm
  expr: Radius1 = Sketch.Constraints.oRingR1 + Sketch.Constraints.oRingR2
  expr: .AttachmentOffset.Base.z = <<oRingHolder>>.Height / 2
FEATURE [PartDesign::Body] Body004  label="plungerHead"
  Group = -> [Cylinder019,Box016,Box017,Cylinder020,Torus]
  Origin = -> Origin004
  Placement = pos=(0,-48,0) rot=(0,0,1;0rad)
  Tip = -> Torus
FEATURE [PartDesign::AdditiveBox] Box018  label="band_holder_body_l"
  AttacherType = Attacher::AttachEngine3D
  AttachmentOffset = pos=(13.85,-2.5,0) rot=(0,0,1;0rad)
  BaseFeature = -> PolarPattern001
  Height = 15
  Length = 10
  MapMode = 5
  Placement = pos=(13.85,6e-16,-2.5) rot=(1,0,0;1.5708rad)
  Refine = true
  Support = -> [XZ_Plane]
  Width = 5
  expr: .AttachmentOffset.Base.x = <<air_chamber>>.Radius + 0.1mm
  expr: .AttachmentOffset.Base.y = -Width / 2
FEATURE [PartDesign::Mirrored] Mirrored008
  BaseFeature = -> Box018
  MirrorPlane = -> YZ_Plane
  Originals = -> [Box018]
  Placement = pos=(13.85,1e-15,-2.5) rot=(1,0,0;1.5708rad)
  Refine = true
FEATURE [PartDesign::SubtractiveCylinder] Cylinder022  label="band_holder_l"
  Angle = 90
  AttacherType = Attacher::AttachEngine3D
  AttachmentOffset = pos=(8,0,0) rot=(0,1,0;3.14159rad)
  BaseFeature = -> Mirrored008
  Height = 5
  MapMode = 7
  Placement = pos=(15.85,-15,-2.5) rot=(0,0,1;0rad)
  Radius = 4
  Refine = true
  Support = -> [Mirrored008]
  expr: Height = <<band_holder_body_l>>.Width
  expr: .AttachmentOffset.Base.x = <<band_holder_body_l>>.Length - Sketch.Constraints.wallThickness
FEATURE [PartDesign::Mirrored] Mirrored009
  BaseFeature = -> Cylinder022
  MirrorPlane = -> YZ_Plane
  Originals = -> [Cylinder022]
  Placement = pos=(15.85,-15,-2.5) rot=(0,0,1;0rad)
  Refine = true
FEATURE [PartDesign::Fillet] Fillet017
  Base = -> Mirrored009 [Edge104,Edge132,Edge97,Edge101,Edge103,Edge98,Edge80,Edge83,Edge82,Edge87,Edge88,Edge130,Edge93,Edge89,Edge57,Edge95]
  BaseFeature = -> Mirrored009
  Placement = pos=(15.85,-15,-2.5) rot=(0,0,1;0rad)
  Radius = 1
  Refine = true
  SupportTransform = false
FEATURE [PartDesign::Fillet] Fillet018
  Base = -> Fillet017 [Edge22,Edge32]
  BaseFeature = -> Fillet017
  Placement = pos=(15.85,-15,-2.5) rot=(0,0,1;0rad)
  Radius = 6
  Refine = true
  SupportTransform = false
FEATURE [PartDesign::Body] Body  label="body"
  Group = -> [Cylinder001,Box,Sphere,Sphere002,Cylinder,Cylinder002,Cylinder003,Cylinder004,Sphere003,Cylinder005,Sphere004,Cylinder006,PolarPattern,Cylinder007,PolarPattern001,Box018,Mirrored008,Cylinder022,Mirrored009,Fillet017,Fillet018]
  Origin = -> Origin
  Tip = -> Fillet018
FEATURE [PartDesign::AdditiveBox] Box019  label="plungerBandHolder"
  AttacherType = Attacher::AttachEngine3D
  AttachmentOffset = pos=(-23.85,0,-4.5) rot=(0,0,1;0rad)
  BaseFeature = -> Cylinder021
  Height = 9
  Length = 47.7
  MapMode = 5
  Placement = pos=(-23.85,0,-4.5) rot=(0,0,1;0rad)
  Refine = true
  Support = -> [XY_Plane003]
  Width = 12
  expr: Length = (<<air_chamber>>.Radius + 0.1mm + <<band_holder_body_l>>.Length) * 2
  expr: Height = <<plungerBody>>.Width
  expr: .AttachmentOffset.Base.z = -Height / 2
  expr: .AttachmentOffset.Base.x = -Length / 2
FEATURE [PartDesign::SubtractiveCylinder] Cylinder024
  Angle = 90
  AttacherType = Attacher::AttachEngine3D
  AttachmentOffset = pos=(8,0,0) rot=(-0.707107,0.707107,0;3.14159rad)
  BaseFeature = -> Box019
  Height = 9
  MapMode = 7
  Placement = pos=(15.85,12,-4.5) rot=(0,0,1;4.71239rad)
  Radius = 4
  Refine = true
  Support = -> [Box019]
  expr: .AttachmentOffset.Base.x = <<band_holder_body_l>>.Length - Sketch.Constraints.wallThickness
  expr: Height = <<plungerBody>>.Width
  expr: Radius = <<band_holder_l>>.Radius
FEATURE [PartDesign::Mirrored] Mirrored010
  BaseFeature = -> Cylinder024
  MirrorPlane = -> YZ_Plane003
  Originals = -> [Cylinder024]
  Placement = pos=(15.85,12,-4.5) rot=(0,0,1;4.71239rad)
  Refine = true
FEATURE [PartDesign::Fillet] Fillet
  Base = -> Mirrored010 [Edge9,Edge21,Edge32,Edge10,Edge39,Edge31,Edge12,Edge13,Edge42,Edge29,Edge28,Edge43,Edge3,Edge14,Edge27,Edge8,Edge20,Edge40]
  BaseFeature = -> Mirrored010
  Placement = pos=(15.85,12,-4.5) rot=(0,0,1;4.71239rad)
  Radius = 1
  Refine = true
  SupportTransform = false
FEATURE [PartDesign::Fillet] Fillet019
  Base = -> Fillet [Edge54,Edge3]
  BaseFeature = -> Fillet
  Placement = pos=(15.85,12,-4.5) rot=(0,0,1;4.71239rad)
  Radius = 8
  Refine = true
  SupportTransform = false
FEATURE [PartDesign::Body] Body003  label="plunger"
  Group = -> [Box002,Wedge,Cylinder021,Box019,Cylinder024,Mirrored010,Fillet,Fillet019]
  Origin = -> Origin003
  Placement = pos=(0,52,0) rot=(0,0,1;0rad)
  Tip = -> Fillet019
FEATURE [PartDesign::AdditiveCylinder] Cylinder026  label="dart_holder_body001"
  Angle = 360
  AttacherType = Attacher::AttachEngine3D
  AttachmentOffset = pos=(0,27.5,0) rot=(0,0,1;0rad)
  Height = 60
  MapMode = 5
  Placement = pos=(0,-6.1e-15,27.5) rot=(1,0,0;1.5708rad)
  Radius = 8.75
  Support = -> [XZ_Plane005]
  expr: Height = Sketch.Constraints.bodyLength + Sketch.Constraints.holderOffset
  expr: Radius = Sketch.Constraints.rDartHolderOutside
  expr: .AttachmentOffset.Base.y = Sketch.Constraints.chamberToHolder
FEATURE [PartDesign::AdditiveBox] Box020  label="chamber_holder_connector001"
  AttacherType = Attacher::AttachEngine3D
  AttachmentOffset = pos=(-8.75,0,-60) rot=(0,0,1;0rad)
  BaseFeature = -> Cylinder026
  Height = 60
  Length = 17.5
  MapMode = 5
  Placement = pos=(-8.75,-60,27.5) rot=(-1,0,0;1.5708rad)
  Support = -> [Cylinder026]
  Width = 27.5
  expr: Width = Sketch.Constraints.chamberToHolder
  expr: Height = Cylinder026.Height
  expr: .AttachmentOffset.Base.z = -Cylinder026.Height
  expr: .AttachmentOffset.Base.x = -Cylinder026.Radius
  expr: Length = Cylinder026.Radius * 2
FEATURE [PartDesign::AdditiveSphere] Sphere006  label="chamber_butt001"
  Angle1 = -90
  Angle2 = 90
  Angle3 = 180
  AttacherType = Attacher::AttachEngine3D
  AttachmentOffset = pos=(-8.75,5,0) rot=(0,0,-1;3.14159rad)
  BaseFeature = -> Box020
  MapMode = 5
  Placement = pos=(0,-55,-1.31e-14) rot=(-1,0,0;3.14159rad)
  Radius = 15.75
  Support = -> [Box020]
  expr: Radius = Sketch.Constraints.rAirChamberOutside
  expr: .AttachmentOffset.Base.x = -Cylinder026.Radius
  expr: .AttachmentOffset.Base.y = Sketch.Constraints.holderOffset
FEATURE [PartDesign::AdditiveSphere] Sphere007  label="holder_butt001"
  Angle1 = -90
  Angle2 = 90
  Angle3 = 360
  AttacherType = Attacher::AttachEngine3D
  BaseFeature = -> Sphere006
  MapMode = 11
  Placement = pos=(0,-60,27.5) rot=(0.57735,-0.57735,0.57735;2.0944rad)
  Radius = 8.75
  Support = -> [Cylinder026]
  expr: Radius = Cylinder026.Radius
FEATURE [PartDesign::AdditiveCylinder] Cylinder033  label="butt_connector001"
  Angle = 180
  AttacherType = Attacher::AttachEngine3D
  AttachmentOffset = pos=(-8.75,0,-27.5) rot=(0,0,1;3.14159rad)
  BaseFeature = -> Sphere007
  Height = 27.5
  MapMode = 5
  Placement = pos=(0,-60,27.5) rot=(1,0,0;3.14159rad)
  Radius = 8.75
  Support = -> [Box020]
  expr: .AttachmentOffset.Base.z = -Box020.Width
  expr: Height = Box020.Width
  expr: Radius = Sphere007.Radius
  expr: .AttachmentOffset.Base.x = -Radius
FEATURE [PartDesign::AdditiveCylinder] Cylinder027  label="air_chamber_body001"
  Angle = 360
  AttacherType = Attacher::AttachEngine3D
  BaseFeature = -> Cylinder033
  Height = 55
  MapMode = 2
  Placement = pos=(0,0,0) rot=(1,0,0;1.5708rad)
  Radius = 15.75
  Support = -> [Sketch]
  expr: Height = Sketch.Constraints.bodyLength
  expr: Radius = Sketch.Constraints.rAirChamberOutside
FEATURE [PartDesign::SubtractiveCylinder] Cylinder031  label="air_chamber001"
  Angle = 360
  AttacherType = Attacher::AttachEngine3D
  BaseFeature = -> Cylinder027
  Height = 55
  MapMode = 2
  Placement = pos=(0,0,0) rot=(1,0,0;1.5708rad)
  Radius = 13.75
  Support = -> [Sketch]
  expr: Height = Cylinder026.Height - Sketch.Constraints.holderOffset
  expr: Radius = Sketch.Constraints.rAirChamber
FEATURE [PartDesign::SubtractiveCylinder] Cylinder025  label="butt_connector_channel001"
  Angle = 180
  AttacherType = Attacher::AttachEngine3D
  BaseFeature = -> Cylinder031
  Height = 27.5
  MapMode = 2
  Placement = pos=(0,-60,27.5) rot=(1,0,0;3.14159rad)
  Radius = 6.75
  Support = -> [Cylinder033]
  expr: Height = Cylinder033.Height
  expr: Radius = Cylinder033.Radius - 2mm
FEATURE [PartDesign::SubtractiveSphere] Sphere005
  Angle1 = -90
  Angle2 = 90
  Angle3 = 180
  AttacherType = Attacher::AttachEngine3D
  BaseFeature = -> Cylinder025
  MapMode = 2
  Placement = pos=(0,-55,-1.31e-14) rot=(1,0,0;3.14159rad)
  Radius = 13.75
  Support = -> [Sphere006]
  expr: Radius = Sketch.Constraints.rAirChamber
FEATURE [PartDesign::SubtractiveCylinder] Cylinder028  label="dart_holder001"
  Angle = 360
  AttacherType = Attacher::AttachEngine3D
  AttachmentOffset = pos=(0,0,-60) rot=(0,0,1;0rad)
  BaseFeature = -> Sphere005
  Height = 60
  MapMode = 5
  Placement = pos=(0,-60,27.5) rot=(-1,0,0;1.5708rad)
  Radius = 6.75
  Support = -> [Cylinder026]
  expr: .AttachmentOffset.Base.z = -Cylinder026.Height
  expr: Height = Cylinder026.Height
  expr: Radius = Cylinder026.Radius - 2mm
FEATURE [PartDesign::SubtractiveSphere] Sphere008
  Angle1 = -90
  Angle2 = 90
  Angle3 = 360
  AttacherType = Attacher::AttachEngine3D
  BaseFeature = -> Cylinder028
  MapMode = 2
  Placement = pos=(0,-60,27.5) rot=(-0.57735,0.57735,-0.57735;4.18879rad)
  Radius = 6.75
  Support = -> [Sphere007]
  expr: Radius = Sphere007.Radius - 2mm
FEATURE [PartDesign::AdditiveCylinder] Cylinder030
  Angle = 360
  AttacherType = Attacher::AttachEngine3D
  BaseFeature = -> Sphere008
  Height = 10
  MapMode = 11
  Placement = pos=(-12.9047,2.9e-15,12.9047) rot=(0.57735,-0.57735,0.57735;2.0944rad)
  Radius = 4.5
  Support = -> [Sketch]
  expr: Radius = Sketch.Constraints.dNutOutside / 2
FEATURE [PartDesign::PolarPattern] PolarPattern005
  Angle = 360
  Axis = -> Y_Axis005
  BaseFeature = -> Cylinder030
  Occurrences = 4
  Originals = -> [Cylinder030]
  Placement = pos=(-12.9047,3e-15,12.9047) rot=(0.57735,-0.57735,0.57735;2.0944rad)
FEATURE [PartDesign::SubtractiveCylinder] Cylinder029
  Angle = 360
  AttacherType = Attacher::AttachEngine3D
  BaseFeature = -> PolarPattern005
  Height = 8
  MapMode = 11
  Placement = pos=(-12.9047,2.9e-15,12.9047) rot=(0.57735,-0.57735,0.57735;2.0944rad)
  Radius = 1.5
  Support = -> [Sketch]
  expr: Height = Cylinder030.Height - 2mm
  expr: Radius = Sketch.Constraints.dInsert / 2
FEATURE [PartDesign::PolarPattern] PolarPattern004
  Angle = 360
  Axis = -> Y_Axis005
  BaseFeature = -> Cylinder029
  Occurrences = 4
  Originals = -> [Cylinder029]
  Placement = pos=(-12.9047,3e-15,12.9047) rot=(0.57735,-0.57735,0.57735;2.0944rad)
FEATURE [PartDesign::AdditiveBox] Box021  label="band_holder_body_l001"
  AttacherType = Attacher::AttachEngine3D
  AttachmentOffset = pos=(13.85,-2.5,0) rot=(0,0,1;0rad)
  BaseFeature = -> PolarPattern004
  Height = 15
  Length = 10
  MapMode = 5
  Placement = pos=(13.85,6e-16,-2.5) rot=(1,0,0;1.5708rad)
  Refine = true
  Support = -> [XZ_Plane005]
  Width = 5
  expr: .AttachmentOffset.Base.y = -Width / 2
  expr: .AttachmentOffset.Base.x = <<air_chamber001>>.Radius + 0.1mm
FEATURE [PartDesign::Mirrored] Mirrored011
  BaseFeature = -> Box021
  MirrorPlane = -> YZ_Plane005
  Originals = -> [Box021]
  Placement = pos=(13.85,1e-15,-2.5) rot=(1,0,0;1.5708rad)
  Refine = true
FEATURE [PartDesign::SubtractiveCylinder] Cylinder032  label="band_holder_l001"
  Angle = 90
  AttacherType = Attacher::AttachEngine3D
  AttachmentOffset = pos=(8,0,0) rot=(0,1,0;3.14159rad)
  BaseFeature = -> Mirrored011
  Height = 5
  MapMode = 7
  Placement = pos=(15.85,-15,-2.5) rot=(0,0,1;0rad)
  Radius = 4
  Refine = true
  Support = -> [Mirrored011]
  expr: .AttachmentOffset.Base.x = <<band_holder_body_l001>>.Length - Sketch.Constraints.wallThickness
  expr: Height = <<band_holder_body_l001>>.Width
FEATURE [PartDesign::Mirrored] Mirrored012
  BaseFeature = -> Cylinder032
  MirrorPlane = -> YZ_Plane005
  Originals = -> [Cylinder032]
  Placement = pos=(15.85,-15,-2.5) rot=(0,0,1;0rad)
  Refine = true
FEATURE [PartDesign::Fillet] Fillet021
  Base = -> Mirrored012 [Edge108,Edge98,Edge91,Edge134,Edge83,Edge93,Edge87,Edge104,Edge132,Edge103,Edge101,Edge97,Edge94,Edge57,Edge82,Edge130,Edge89,Edge88,Edge79]
  BaseFeature = -> Mirrored012
  Placement = pos=(15.85,-15,-2.5) rot=(0,0,1;0rad)
  Radius = 1
  Refine = true
  SupportTransform = false
FEATURE [PartDesign::Fillet] Fillet020
  Base = -> Fillet021 [Edge22,Edge32]
  BaseFeature = -> Fillet021
  Placement = pos=(15.85,-15,-2.5) rot=(0,0,1;0rad)
  Radius = 6
  Refine = true
  SupportTransform = false
FEATURE [PartDesign::AdditiveWedge] Wedge005
  AttacherType = Attacher::AttachEngine3D
  AttachmentOffset = pos=(-1.5,34.25,0) rot=(0,0,1;0rad)
  BaseFeature = -> Fillet020
  MapMode = 5
  Placement = pos=(-1.5,-7.6e-15,34.25) rot=(1,0,0;1.5708rad)
  Refine = true
  Support = -> [XZ_Plane005]
  X2max = 1.5
  X2min = 1.5
  Xmax = 3
  Xmin = 0
  Ymax = 5
  Ymin = 0
  Z2max = 1
  Z2min = 0
  Zmax = 4
  Zmin = 0
  expr: X2max = Xmax / 2
  expr: X2min = Xmax / 2
  expr: .AttachmentOffset.Base.x = -Xmax / 2 - Xmin / 2
  expr: .AttachmentOffset.Base.y = Sketch.Constraints.chamberToHolder + <<dart_holder001>>.Radius
  expr: Ymax = Sketch.Constraints.wallThickness + 3mm
FEATURE [PartDesign::AdditiveWedge] Wedge006
  AttacherType = Attacher::AttachEngine3D
  AttachmentOffset = pos=(3,34.25,60) rot=(0,1,0;3.14159rad)
  BaseFeature = -> Wedge005
  MapMode = 5
  Placement = pos=(3,-60,34.25) rot=(0,0.707107,0.707107;3.14159rad)
  Refine = true
  Support = -> [XZ_Plane005]
  X2max = 6
  X2min = 0
  Xmax = 6
  Xmin = 0
  Ymax = 5
  Ymin = 0
  Z2max = 1
  Z2min = 0
  Zmax = 8
  Zmin = 0
  expr: Ymax = Wedge005.Ymax
  expr: X2max = Xmax
  expr: .AttachmentOffset.Base.z = <<dart_holder001>>.Height
  expr: .AttachmentOffset.Base.y = Sketch.Constraints.chamberToHolder + <<dart_holder001>>.Radius
  expr: .AttachmentOffset.Base.x = Xmax / 2 + Xmin / 2
FEATURE [PartDesign::SubtractiveWedge] Wedge007
  AttacherType = Attacher::AttachEngine3D
  AttachmentOffset = pos=(0,0,-2) rot=(1,0,0;3.14159rad)
  BaseFeature = -> Wedge006
  MapMode = 7
  Placement = pos=(1,-60,39.25) rot=(0.57735,0.57735,-0.57735;4.18879rad)
  Refine = true
  Support = -> [Wedge006]
  X2max = 3
  X2min = 0
  Xmax = 3
  Xmin = 0
  Ymax = 1
  Ymin = 0
  Z2max = 1
  Z2min = 1
  Zmax = 2
  Zmin = 0
  expr: X2max = Xmax
  expr: Z2max = Zmax / 2
  expr: Z2min = Zmax / 2
  expr: .AttachmentOffset.Base.z = -Wedge006.Xmax / 2 + Zmax / 2
FEATURE [PartDesign::Body] Body005  label="bodyWithSight"
  Group = -> [Cylinder026,Box020,Sphere006,Sphere007,Cylinder033,Cylinder027,Cylinder031,Cylinder025,Sphere005,Cylinder028,Sphere008,Cylinder030,PolarPattern005,Cylinder029,PolarPattern004,Box021,Mirrored011,Cylinder032,Mirrored012,Fillet021,Fillet020,Wedge005,Wedge006,Wedge007]
  Origin = -> Origin005
  Tip = -> Wedge007
FEATURE [PartDesign::AdditiveBox] Box022  label="plungerBody001"
  AttacherType = Attacher::AttachEngine3D
  AttachmentOffset = pos=(-4.5,-4.5,0) rot=(0,0,1;0rad)
  Height = 64
  Length = 9
  MapMode = 5
  Placement = pos=(-4.5,1e-15,-4.5) rot=(1,0,0;1.5708rad)
  Refine = true
  Support = -> [XZ_Plane006]
  Width = 9
  expr: Height = Sketch.Constraints.bodyLength + 9mm
  expr: Width = Sketch.Constraints.capHoleWidth - 1mm
  expr: Length = Sketch.Constraints.capHoleLength - 1mm
  expr: .AttachmentOffset.Base.y = -Width / 2
  expr: .AttachmentOffset.Base.x = -Length / 2
FEATURE [PartDesign::SubtractiveWedge] Wedge008
  AttacherType = Attacher::AttachEngine3D
  AttachmentOffset = pos=(-9,43,-2) rot=(0,0,1;0rad)
  BaseFeature = -> Box022
  MapMode = 5
  Placement = pos=(4.5,-43,2.5) rot=(0,0,1;3.14159rad)
  Refine = true
  Support = -> [Box022]
  X2max = 9
  X2min = 0
  Xmax = 9
  Xmin = 0
  Ymax = 4
  Ymin = 0
  Z2max = 2
  Z2min = 2
  Zmax = 2
  Zmin = 0
  expr: .AttachmentOffset.Base.x = -Xmax / 2 - Box022.Length / 2
  expr: .AttachmentOffset.Base.y = Box022.Height - Sketch.Constraints.plungerHeadSpace
  expr: Xmax = <<plungerBody001>>.Length
  expr: X2max = Xmax
FEATURE [PartDesign::SubtractiveCylinder] Cylinder035
  Angle = 360
  AttacherType = Attacher::AttachEngine3D
  AttachmentOffset = pos=(0,-55.5,-4.5) rot=(0,0,1;0rad)
  BaseFeature = -> Wedge008
  Height = 9
  MapMode = 5
  Placement = pos=(0,-55.5,-4.5) rot=(0,0,1;0rad)
  Radius = 1.5
  Refine = true
  Support = -> [XY_Plane006]
  expr: Height = <<plungerBody001>>.Width
  expr: Radius = Sketch.Constraints.rInsert
  expr: .AttachmentOffset.Base.z = -<<plungerBody001>>.Width / 2
  expr: .AttachmentOffset.Base.y = -<<plungerBody001>>.Height + Box017.Height - <<plungerConnector>>.Height / 2
FEATURE [PartDesign::AdditiveBox] Box023  label="plungerBandHolder001"
  AttacherType = Attacher::AttachEngine3D
  AttachmentOffset = pos=(-23.85,0,-4.5) rot=(0,0,1;0rad)
  BaseFeature = -> Cylinder035
  Height = 9
  Length = 47.7
  MapMode = 5
  Placement = pos=(-23.85,0,-4.5) rot=(0,0,1;0rad)
  Refine = true
  Support = -> [XY_Plane006]
  Width = 12
  expr: .AttachmentOffset.Base.x = -Length / 2
  expr: .AttachmentOffset.Base.z = -Height / 2
  expr: Height = <<plungerBody001>>.Width
  expr: Length = (<<air_chamber>>.Radius + 0.1mm + <<band_holder_body_l>>.Length) * 2
FEATURE [PartDesign::SubtractiveCylinder] Cylinder034
  Angle = 90
  AttacherType = Attacher::AttachEngine3D
  AttachmentOffset = pos=(8,0,0) rot=(-0.707107,0.707107,0;3.14159rad)
  BaseFeature = -> Box023
  Height = 9
  MapMode = 7
  Placement = pos=(15.85,12,-4.5) rot=(0,0,1;4.71239rad)
  Radius = 4
  Refine = true
  Support = -> [Box023]
  expr: Radius = <<band_holder_l>>.Radius
  expr: Height = <<plungerBody001>>.Width
  expr: .AttachmentOffset.Base.x = <<band_holder_body_l>>.Length - Sketch.Constraints.wallThickness
FEATURE [PartDesign::Mirrored] Mirrored013
  BaseFeature = -> Cylinder034
  MirrorPlane = -> YZ_Plane006
  Originals = -> [Cylinder034]
  Placement = pos=(15.85,12,-4.5) rot=(0,0,1;4.71239rad)
  Refine = true
FEATURE [PartDesign::Fillet] Fillet023
  Base = -> Mirrored013 [Edge9,Edge21,Edge32,Edge10,Edge39,Edge31,Edge12,Edge13,Edge42,Edge29,Edge28,Edge43,Edge3,Edge14,Edge27,Edge8,Edge20,Edge40]
  BaseFeature = -> Mirrored013
  Placement = pos=(15.85,12,-4.5) rot=(0,0,1;4.71239rad)
  Radius = 1
  Refine = true
  SupportTransform = false
FEATURE [PartDesign::Fillet] Fillet022
  Base = -> Fillet023 [Edge54,Edge3]
  BaseFeature = -> Fillet023
  Placement = pos=(15.85,12,-4.5) rot=(0,0,1;4.71239rad)
  Radius = 8
  Refine = true
  SupportTransform = false
FEATURE [PartDesign::AdditiveBox] Box024  label="plungerHandleSpacer"
  AttacherType = Attacher::AttachEngine3D
  AttachmentOffset = pos=(-4.5,12,-4.5) rot=(0,0,1;0rad)
  BaseFeature = -> Fillet022
  Height = 9
  Length = 9
  MapMode = 5
  Placement = pos=(-4.5,12,-4.5) rot=(0,0,1;0rad)
  Refine = true
  Support = -> [XY_Plane003]
  Width = 10
  expr: .AttachmentOffset.Base.y = <<plungerBandHolder>>.Width
  expr: .AttachmentOffset.Base.x = -Length / 2
  expr: Length = <<plungerBody>>.Length
  expr: .AttachmentOffset.Base.z = -Height / 2
  expr: Height = <<plungerBody>>.Width
FEATURE [PartDesign::AdditiveBox] Box025  label="plungerHandle"
  AttacherType = Attacher::AttachEngine3D
  AttachmentOffset = pos=(-23.85,22,-4.5) rot=(0,0,1;0rad)
  BaseFeature = -> Box024
  Height = 9
  Length = 47.7
  MapMode = 5
  Placement = pos=(-23.85,22,-4.5) rot=(0,0,1;0rad)
  Refine = true
  Support = -> [XY_Plane006]
  Width = 14
  expr: .AttachmentOffset.Base.z = -Height / 2
  expr: .AttachmentOffset.Base.x = -Length / 2
  expr: Height = <<plungerBody>>.Width
  expr: Length = <<plungerBandHolder001>>.Length
  expr: .AttachmentOffset.Base.y = <<plungerBandHolder>>.Width + <<plungerHandleSpacer>>.Width
FEATURE [PartDesign::SubtractiveCylinder] Cylinder036
  Angle = 180
  AttacherType = Attacher::AttachEngine3D
  AttachmentOffset = pos=(11.35,0,0) rot=(0,1,0;3.14159rad)
  BaseFeature = -> Box025
  Height = 9
  MapMode = 7
  Placement = pos=(12.5,22,-4.5) rot=(0,0,1;0rad)
  Radius = 8
  Refine = true
  Support = -> [Box025]
  expr: .AttachmentOffset.Base.x = <<plungerHandle>>.Length / 2 - <<plungerHandleSpacer>>.Length / 2 - Radius
  expr: Height = <<plungerBody>>.Width
FEATURE [PartDesign::Mirrored] Mirrored014
  BaseFeature = -> Cylinder036
  MirrorPlane = -> YZ_Plane006
  Originals = -> [Cylinder036]
  Placement = pos=(12.5,22,-4.5) rot=(0,0,1;0rad)
  Refine = true
FEATURE [PartDesign::Fillet] Fillet024
  Base = -> Mirrored014 [Edge91,Edge47,Edge10,Edge29,Edge92,Edge45,Edge42,Edge46,Edge9,Edge94,Edge93,Edge30]
  BaseFeature = -> Mirrored014
  Placement = pos=(12.5,22,-4.5) rot=(0,0,1;0rad)
  Radius = 1
  Refine = true
  SupportTransform = false
FEATURE [PartDesign::Fillet] Fillet025
  Base = -> Fillet024 [Edge36,Edge32]
  BaseFeature = -> Fillet024
  Placement = pos=(12.5,22,-4.5) rot=(0,0,1;0rad)
  Radius = 6
  Refine = true
  SupportTransform = false
FEATURE [PartDesign::Body] Body006  label="plungerWithHandle"
  Group = -> [Box022,Wedge008,Cylinder035,Box023,Cylinder034,Mirrored013,Fillet023,Fillet022,Box024,Box025,Cylinder036,Mirrored014,Fillet024,Fillet025]
  Origin = -> Origin006
  Placement = pos=(0,11,0) rot=(0,0,1;0rad)
  Tip = -> Fillet025
FEATURE [PartDesign::AdditiveCylinder] Cylinder037  label="dart_holder_body002"
  Angle = 360
  AttacherType = Attacher::AttachEngine3D
  AttachmentOffset = pos=(0,27.5,0) rot=(0,0,1;0rad)
  Height = 60
  MapMode = 5
  Placement = pos=(0,-6.1e-15,27.5) rot=(1,0,0;1.5708rad)
  Radius = 8.75
  Support = -> [XZ_Plane007]
  expr: Height = Sketch.Constraints.bodyLength + Sketch.Constraints.holderOffset
  expr: Radius = Sketch.Constraints.rDartHolderOutside
  expr: .AttachmentOffset.Base.y = Sketch.Constraints.chamberToHolder
FEATURE [PartDesign::AdditiveBox] Box026  label="chamber_holder_connector002"
  AttacherType = Attacher::AttachEngine3D
  AttachmentOffset = pos=(-8.75,0,-60) rot=(0,0,1;0rad)
  BaseFeature = -> Cylinder037
  Height = 60
  Length = 17.5
  MapMode = 5
  Placement = pos=(-8.75,-60,27.5) rot=(-1,0,0;1.5708rad)
  Support = -> [Cylinder037]
  Width = 27.5
  expr: Width = Sketch.Constraints.chamberToHolder
  expr: Height = Cylinder037.Height
  expr: .AttachmentOffset.Base.z = -Cylinder037.Height
  expr: .AttachmentOffset.Base.x = -Cylinder037.Radius
  expr: Length = Cylinder037.Radius * 2
FEATURE [PartDesign::AdditiveSphere] Sphere009  label="chamber_butt002"
  Angle1 = -90
  Angle2 = 90
  Angle3 = 180
  AttacherType = Attacher::AttachEngine3D
  AttachmentOffset = pos=(-8.75,5,0) rot=(0,0,-1;3.14159rad)
  BaseFeature = -> Box026
  MapMode = 5
  Placement = pos=(0,-55,-1.31e-14) rot=(-1,0,0;3.14159rad)
  Radius = 15.75
  Support = -> [Box026]
  expr: Radius = Sketch.Constraints.rAirChamberOutside
  expr: .AttachmentOffset.Base.x = -Cylinder037.Radius
  expr: .AttachmentOffset.Base.y = Sketch.Constraints.holderOffset
FEATURE [PartDesign::AdditiveSphere] Sphere010  label="holder_butt002"
  Angle1 = -90
  Angle2 = 90
  Angle3 = 360
  AttacherType = Attacher::AttachEngine3D
  BaseFeature = -> Sphere009
  MapMode = 11
  Placement = pos=(0,-60,27.5) rot=(0.57735,-0.57735,0.57735;2.0944rad)
  Radius = 8.75
  Support = -> [Cylinder037]
  expr: Radius = Cylinder037.Radius
FEATURE [PartDesign::AdditiveCylinder] Cylinder038  label="butt_connector002"
  Angle = 180
  AttacherType = Attacher::AttachEngine3D
  AttachmentOffset = pos=(-8.75,0,-27.5) rot=(0,0,1;3.14159rad)
  BaseFeature = -> Sphere010
  Height = 27.5
  MapMode = 5
  Placement = pos=(0,-60,27.5) rot=(1,0,0;3.14159rad)
  Radius = 8.75
  Support = -> [Box026]
  expr: .AttachmentOffset.Base.z = -Box026.Width
  expr: Height = Box026.Width
  expr: Radius = Sphere010.Radius
  expr: .AttachmentOffset.Base.x = -Radius
FEATURE [PartDesign::AdditiveCylinder] Cylinder039  label="air_chamber_body002"
  Angle = 360
  AttacherType = Attacher::AttachEngine3D
  BaseFeature = -> Cylinder038
  Height = 55
  MapMode = 2
  Placement = pos=(0,0,0) rot=(1,0,0;1.5708rad)
  Radius = 15.75
  Support = -> [Sketch]
  expr: Height = Sketch.Constraints.bodyLength
  expr: Radius = Sketch.Constraints.rAirChamberOutside
FEATURE [PartDesign::Body] Body007  label="cutBody"
  Group = -> [Cylinder037,Box026,Sphere009,Sphere010,Cylinder038,Cylinder039]
  Origin = -> Origin007
  Tip = -> Fillet018
FEATURE [PartDesign::AdditiveCylinder] Cylinder042  label="dart_holder_body003"
  Angle = 360
  AttacherType = Attacher::AttachEngine3D
  AttachmentOffset = pos=(0,27.5,0) rot=(0,0,1;0rad)
  Height = 60
  MapMode = 5
  Placement = pos=(0,-6.1e-15,27.5) rot=(1,0,0;1.5708rad)
  Radius = 8.75
  Support = -> [XZ_Plane008]
  expr: .AttachmentOffset.Base.y = Sketch.Constraints.chamberToHolder
  expr: Radius = Sketch.Constraints.rDartHolderOutside
  expr: Height = Sketch.Constraints.bodyLength + Sketch.Constraints.holderOffset
FEATURE [PartDesign::AdditiveBox] Box027  label="chamber_holder_connector003"
  AttacherType = Attacher::AttachEngine3D
  AttachmentOffset = pos=(-8.75,0,-60) rot=(0,0,1;0rad)
  BaseFeature = -> Cylinder042
  Height = 60
  Length = 17.5
  MapMode = 5
  Placement = pos=(-8.75,-60,27.5) rot=(-1,0,0;1.5708rad)
  Support = -> [Cylinder042]
  Width = 27.5
  expr: Length = Cylinder042.Radius * 2
  expr: .AttachmentOffset.Base.x = -Cylinder042.Radius
  expr: .AttachmentOffset.Base.z = -Cylinder042.Height
  expr: Height = Cylinder042.Height
  expr: Width = Sketch.Constraints.chamberToHolder
FEATURE [PartDesign::AdditiveSphere] Sphere013  label="chamber_butt003"
  Angle1 = -90
  Angle2 = 90
  Angle3 = 180
  AttacherType = Attacher::AttachEngine3D
  AttachmentOffset = pos=(-8.75,5,0) rot=(0,0,-1;3.14159rad)
  BaseFeature = -> Box027
  MapMode = 5
  Placement = pos=(0,-55,-1.31e-14) rot=(-1,0,0;3.14159rad)
  Radius = 15.75
  Support = -> [Box027]
  expr: .AttachmentOffset.Base.y = Sketch.Constraints.holderOffset
  expr: .AttachmentOffset.Base.x = -Cylinder042.Radius
  expr: Radius = Sketch.Constraints.rAirChamberOutside
FEATURE [PartDesign::AdditiveSphere] Sphere014  label="holder_butt003"
  Angle1 = -90
  Angle2 = 90
  Angle3 = 360
  AttacherType = Attacher::AttachEngine3D
  BaseFeature = -> Sphere013
  MapMode = 11
  Placement = pos=(0,-60,27.5) rot=(0.57735,-0.57735,0.57735;2.0944rad)
  Radius = 8.75
  Support = -> [Cylinder042]
  expr: Radius = Cylinder042.Radius
FEATURE [PartDesign::AdditiveCylinder] Cylinder048  label="butt_connector003"
  Angle = 180
  AttacherType = Attacher::AttachEngine3D
  AttachmentOffset = pos=(-8.75,0,-27.5) rot=(0,0,1;3.14159rad)
  BaseFeature = -> Sphere014
  Height = 27.5
  MapMode = 5
  Placement = pos=(0,-60,27.5) rot=(1,0,0;3.14159rad)
  Radius = 8.75
  Support = -> [Box027]
  expr: .AttachmentOffset.Base.x = -Radius
  expr: Radius = Sphere014.Radius
  expr: Height = Box027.Width
  expr: .AttachmentOffset.Base.z = -Box027.Width
FEATURE [PartDesign::AdditiveCylinder] Cylinder045  label="air_chamber_body003"
  Angle = 360
  AttacherType = Attacher::AttachEngine3D
  BaseFeature = -> Cylinder048
  Height = 55
  MapMode = 2
  Placement = pos=(0,0,0) rot=(1,0,0;1.5708rad)
  Radius = 15.75
  Support = -> [Sketch]
  expr: Radius = Sketch.Constraints.rAirChamberOutside
  expr: Height = Sketch.Constraints.bodyLength
FEATURE [PartDesign::SubtractiveCylinder] Cylinder040  label="air_chamber002"
  Angle = 360
  AttacherType = Attacher::AttachEngine3D
  BaseFeature = -> Cylinder045
  Height = 55
  MapMode = 2
  Placement = pos=(0,0,0) rot=(1,0,0;1.5708rad)
  Radius = 13.75
  Support = -> [Sketch]
  expr: Radius = Sketch.Constraints.rAirChamber
  expr: Height = Cylinder042.Height - Sketch.Constraints.holderOffset
FEATURE [PartDesign::SubtractiveCylinder] Cylinder044  label="butt_connector_channel002"
  Angle = 180
  AttacherType = Attacher::AttachEngine3D
  BaseFeature = -> Cylinder040
  Height = 27.5
  MapMode = 2
  Placement = pos=(0,-60,27.5) rot=(1,0,0;3.14159rad)
  Radius = 6.75
  Support = -> [Cylinder048]
  expr: Radius = Cylinder048.Radius - 2mm
  expr: Height = Cylinder048.Height
FEATURE [PartDesign::SubtractiveSphere] Sphere012
  Angle1 = -90
  Angle2 = 90
  Angle3 = 180
  AttacherType = Attacher::AttachEngine3D
  BaseFeature = -> Cylinder044
  MapMode = 2
  Placement = pos=(0,-55,-1.31e-14) rot=(1,0,0;3.14159rad)
  Radius = 13.75
  Support = -> [Sphere013]
  expr: Radius = Sketch.Constraints.rAirChamber
FEATURE [PartDesign::SubtractiveCylinder] Cylinder043  label="dart_holder002"
  Angle = 360
  AttacherType = Attacher::AttachEngine3D
  AttachmentOffset = pos=(0,0,-60) rot=(0,0,1;0rad)
  BaseFeature = -> Sphere012
  Height = 60
  MapMode = 5
  Placement = pos=(0,-60,27.5) rot=(-1,0,0;1.5708rad)
  Radius = 6.75
  Support = -> [Cylinder042]
  expr: Radius = Cylinder042.Radius - 2mm
  expr: Height = Cylinder042.Height
  expr: .AttachmentOffset.Base.z = -Cylinder042.Height
FEATURE [PartDesign::SubtractiveSphere] Sphere011
  Angle1 = -90
  Angle2 = 90
  Angle3 = 360
  AttacherType = Attacher::AttachEngine3D
  BaseFeature = -> Cylinder043
  MapMode = 2
  Placement = pos=(0,-60,27.5) rot=(-0.57735,0.57735,-0.57735;4.18879rad)
  Radius = 6.75
  Support = -> [Sphere014]
  expr: Radius = Sphere014.Radius - 2mm
FEATURE [PartDesign::AdditiveCylinder] Cylinder047
  Angle = 360
  AttacherType = Attacher::AttachEngine3D
  BaseFeature = -> Sphere011
  Height = 10
  MapMode = 11
  Placement = pos=(-12.9047,2.9e-15,12.9047) rot=(0.57735,-0.57735,0.57735;2.0944rad)
  Radius = 4.5
  Support = -> [Sketch]
  expr: Radius = Sketch.Constraints.dNutOutside / 2
FEATURE [PartDesign::PolarPattern] PolarPattern006
  Angle = 360
  Axis = -> Y_Axis007
  BaseFeature = -> Cylinder047
  Occurrences = 4
  Originals = -> [Cylinder047]
  Placement = pos=(-12.9047,3e-15,12.9047) rot=(0.57735,-0.57735,0.57735;2.0944rad)
FEATURE [PartDesign::SubtractiveCylinder] Cylinder046
  Angle = 360
  AttacherType = Attacher::AttachEngine3D
  BaseFeature = -> PolarPattern006
  Height = 8
  MapMode = 11
  Placement = pos=(-12.9047,2.9e-15,12.9047) rot=(0.57735,-0.57735,0.57735;2.0944rad)
  Radius = 1.5
  Support = -> [Sketch]
  expr: Radius = Sketch.Constraints.dInsert / 2
  expr: Height = Cylinder047.Height - 2mm
FEATURE [PartDesign::PolarPattern] PolarPattern007
  Angle = 360
  Axis = -> Y_Axis007
  BaseFeature = -> Cylinder046
  Occurrences = 4
  Originals = -> [Cylinder046]
  Placement = pos=(-12.9047,3e-15,12.9047) rot=(0.57735,-0.57735,0.57735;2.0944rad)
FEATURE [PartDesign::AdditiveBox] Box028  label="band_holder_body_l002"
  AttacherType = Attacher::AttachEngine3D
  AttachmentOffset = pos=(13.85,-2.5,0) rot=(0,0,1;0rad)
  BaseFeature = -> PolarPattern007
  Height = 15
  Length = 10
  MapMode = 5
  Placement = pos=(13.85,6e-16,-2.5) rot=(1,0,0;1.5708rad)
  Refine = true
  Support = -> [XZ_Plane008]
  Width = 5
  expr: .AttachmentOffset.Base.x = <<air_chamber002>>.Radius + 0.1mm
  expr: .AttachmentOffset.Base.y = -Width / 2
FEATURE [PartDesign::Mirrored] Mirrored015
  BaseFeature = -> Box028
  MirrorPlane = -> YZ_Plane007
  Originals = -> [Box028]
  Placement = pos=(13.85,1e-15,-2.5) rot=(1,0,0;1.5708rad)
  Refine = true
FEATURE [PartDesign::SubtractiveCylinder] Cylinder041  label="band_holder_l002"
  Angle = 90
  AttacherType = Attacher::AttachEngine3D
  AttachmentOffset = pos=(8,0,0) rot=(0,1,0;3.14159rad)
  BaseFeature = -> Mirrored015
  Height = 5
  MapMode = 7
  Placement = pos=(15.85,-15,-2.5) rot=(0,0,1;0rad)
  Radius = 4
  Refine = true
  Support = -> [Mirrored015]
  expr: Height = <<band_holder_body_l002>>.Width
  expr: .AttachmentOffset.Base.x = <<band_holder_body_l002>>.Length - Sketch.Constraints.wallThickness
FEATURE [PartDesign::Mirrored] Mirrored016
  BaseFeature = -> Cylinder041
  MirrorPlane = -> YZ_Plane007
  Originals = -> [Cylinder041]
  Placement = pos=(15.85,-15,-2.5) rot=(0,0,1;0rad)
  Refine = true
FEATURE [PartDesign::Fillet] Fillet026
  Base = -> Mirrored016 [Edge108,Edge98,Edge92,Edge134,Edge83,Edge97,Edge87,Edge132,Edge101,Edge103,Edge104,Edge57,Edge94,Edge89,Edge130,Edge80,Edge82,Edge88]
  BaseFeature = -> Mirrored016
  Placement = pos=(15.85,-15,-2.5) rot=(0,0,1;0rad)
  Radius = 1
  Refine = true
  SupportTransform = false
FEATURE [PartDesign::Fillet] Fillet027
  Base = -> Fillet026 [Edge22,Edge32]
  BaseFeature = -> Fillet026
  Placement = pos=(15.85,-15,-2.5) rot=(0,0,1;0rad)
  Radius = 6
  Refine = true
  SupportTransform = false
FEATURE [PartDesign::AdditiveWedge] Wedge010  label="frontSight"
  AttacherType = Attacher::AttachEngine3D
  AttachmentOffset = pos=(-1.5,34.25,0) rot=(0,0,1;0rad)
  BaseFeature = -> Fillet027
  MapMode = 5
  Placement = pos=(-1.5,-7.6e-15,34.25) rot=(1,0,0;1.5708rad)
  Refine = true
  Support = -> [XZ_Plane008]
  X2max = 1.5
  X2min = 1.5
  Xmax = 3
  Xmin = 0
  Ymax = 8
  Ymin = 0
  Z2max = 1
  Z2min = 0
  Zmax = 4
  Zmin = 0
  expr: Ymax = Sketch.Constraints.wallThickness + Sketch.Constraints.sightHeight
  expr: .AttachmentOffset.Base.y = Sketch.Constraints.chamberToHolder + <<dart_holder002>>.Radius
  expr: .AttachmentOffset.Base.x = -Xmax / 2 - Xmin / 2
  expr: X2min = Xmax / 2
  expr: X2max = Xmax / 2
FEATURE [PartDesign::AdditiveWedge] Wedge009  label="rearSight"
  AttacherType = Attacher::AttachEngine3D
  AttachmentOffset = pos=(3,34.25,60) rot=(0,1,0;3.14159rad)
  BaseFeature = -> Wedge010
  MapMode = 5
  Placement = pos=(3,-60,34.25) rot=(0,0.707107,0.707107;3.14159rad)
  Refine = true
  Support = -> [XZ_Plane008]
  X2max = 6
  X2min = 0
  Xmax = 6
  Xmin = 0
  Ymax = 8
  Ymin = 0
  Z2max = 1
  Z2min = 0
  Zmax = 12
  Zmin = 0
  expr: .AttachmentOffset.Base.x = Xmax / 2 + Xmin / 2
  expr: .AttachmentOffset.Base.y = Sketch.Constraints.chamberToHolder + <<dart_holder002>>.Radius
  expr: .AttachmentOffset.Base.z = <<dart_holder002>>.Height
  expr: X2max = Xmax
  expr: Ymax = <<frontSight>>.Ymax
FEATURE [PartDesign::SubtractiveWedge] Wedge011  label="rearSightCut"
  AttacherType = Attacher::AttachEngine3D
  AttachmentOffset = pos=(0,0,-2) rot=(1,0,0;3.14159rad)
  BaseFeature = -> Wedge009
  MapMode = 7
  Placement = pos=(1,-60,42.25) rot=(0.57735,0.57735,-0.57735;4.18879rad)
  Refine = true
  Support = -> [Wedge009]
  X2max = 9
  X2min = 0
  Xmax = 9
  Xmin = 0
  Ymax = 2
  Ymin = 0
  Z2max = 1
  Z2min = 1
  Zmax = 2
  Zmin = 0
  expr: .AttachmentOffset.Base.z = -Wedge009.Xmax / 2 + Zmax / 2
  expr: Z2min = Zmax / 2
  expr: Z2max = Zmax / 2
  expr: X2max = Xmax
FEATURE [PartDesign::AdditiveBox] Box029
  AttacherType = Attacher::AttachEngine3D
  AttachmentOffset = pos=(-3,-24.75,0) rot=(0,0,1;0rad)
  BaseFeature = -> Wedge011
  Height = 20
  Length = 6
  MapMode = 5
  Placement = pos=(-3,5.5e-15,-24.75) rot=(1,0,0;1.5708rad)
  Refine = true
  Support = -> [XZ_Plane008]
  Width = 11
  expr: Width = 2mm + Sketch.Constraints.triggerPullerLength + Sketch.Constraints.wallThickness
  expr: .AttachmentOffset.Base.y = -<<air_chamber>>.Radius - Width
  expr: .AttachmentOffset.Base.x = -Length / 2
  expr: Length = Sketch.Constraints.triggerPullerWidth + 1mm + 2mm
FEATURE [PartDesign::AdditiveBox] Box030  label="pullerBody"
  AttacherType = Attacher::AttachEngine3D
  AttachmentOffset = pos=(-1.5,-16,0) rot=(0,0,1;0rad)
  Height = 7
  Length = 3
  MapMode = 5
  Placement = pos=(-1.5,-16,0) rot=(0,0,1;0rad)
  Refine = true
  Support = -> [XY_Plane009]
  Width = 36
  expr: .AttachmentOffset.Base.x = -Length / 2
  expr: Length = Sketch.Constraints.triggerPullerWidth
  expr: Height = Sketch.Constraints.triggerPullerLength
  expr: .AttachmentOffset.Base.y = -Sketch.Constraints.pullerSpacing
FEATURE [PartDesign::SubtractiveBox] Box031
  AttacherType = Attacher::AttachEngine3D
  AttachmentOffset = pos=(-2,-23.25,0) rot=(0,0,1;0rad)
  BaseFeature = -> Box029
  Height = 20
  Length = 4
  MapMode = 5
  Placement = pos=(-2,5.2e-15,-23.25) rot=(1,0,0;1.5708rad)
  Refine = true
  Support = -> [XZ_Plane008]
  Width = 7.5
  expr: Length = Sketch.Constraints.triggerPullerWidth + 1mm
  expr: .AttachmentOffset.Base.x = -Length / 2
  expr: Width = Sketch.Constraints.triggerPullerLength + 0.5mm
  expr: Height = <<Box029>>.Height
  expr: .AttachmentOffset.Base.y = -<<air_chamber_body>>.Radius - Width
FEATURE [PartDesign::SubtractiveWedge] Wedge013
  AttacherType = Attacher::AttachEngine3D
  AttachmentOffset = pos=(-1.5,-14,5) rot=(0,0,1;0rad)
  BaseFeature = -> Box030
  MapMode = 5
  Placement = pos=(-1.5,-14,5) rot=(0,0,1;0rad)
  Refine = true
  Support = -> [XY_Plane009]
  X2max = 3
  X2min = 0
  Xmax = 3
  Xmin = 0
  Ymax = 8
  Ymin = 0
  Z2max = 10
  Z2min = -1
  Zmax = 10
  Zmin = 2
  expr: X2max = Xmax
  expr: .AttachmentOffset.Base.y = -Ymax - 6mm
  expr: .AttachmentOffset.Base.x = -Xmax / 2
  expr: .AttachmentOffset.Base.z = <<pullerBody>>.Height - 2mm
  expr: Xmax = <<pullerBody>>.Length
FEATURE [PartDesign::AdditiveBox] Box033
  AttacherType = Attacher::AttachEngine3D
  AttachmentOffset = pos=(-1.5,20,-20) rot=(0,0,1;0rad)
  BaseFeature = -> Wedge013
  Height = 27
  Length = 3
  MapMode = 5
  Placement = pos=(-1.5,20,-20) rot=(0,0,1;0rad)
  Refine = true
  Support = -> [XY_Plane009]
  Width = 15
  expr: .AttachmentOffset.Base.x = -Length / 2
  expr: .AttachmentOffset.Base.y = <<pullerBody>>.Width - Sketch.Constraints.pullerSpacing
  expr: Length = <<pullerBody>>.Length
  expr: .AttachmentOffset.Base.z = <<pullerBody>>.Height - Height
  expr: Height = 20mm + <<pullerBody>>.Height
FEATURE [PartDesign::SubtractiveCylinder] Cylinder049
  Angle = 84
  AttacherType = Attacher::AttachEngine3D
  AttachmentOffset = pos=(11,10,-3) rot=(0,0,1;2.40855rad)
  BaseFeature = -> Box033
  Height = 3
  MapMode = 7
  Placement = pos=(1.5,9,-10) rot=(-0.376764,-0.846226,0.376764;1.737rad)
  Radius = 15
  Refine = true
  Support = -> [Box033]
  expr: .AttachmentOffset.Base.z = -<<Box033>>.Length
  expr: Height = <<Box033>>.Length
  expr: .AttachmentOffset.Rotation.Yaw = 180deg - Angle / 2
FEATURE [PartDesign::Fillet] Fillet028
  Base = -> Cylinder049 [Edge7,Edge33,Edge29,Edge18]
  BaseFeature = -> Cylinder049
  Placement = pos=(1.5,9,-10) rot=(-0.376764,-0.846226,0.376764;1.737rad)
  Radius = 1
  Refine = true
  SupportTransform = false
FEATURE [PartDesign::Fillet] Fillet029
  Base = -> Fillet028 [Edge3]
  BaseFeature = -> Fillet028
  Placement = pos=(1.5,9,-10) rot=(-0.376764,-0.846226,0.376764;1.737rad)
  Radius = 10
  Refine = true
  SupportTransform = false
FEATURE [PartDesign::SubtractiveCylinder] Cylinder050
  Angle = 360
  AttacherType = Attacher::AttachEngine3D
  AttachmentOffset = pos=(1,-3,-3) rot=(0,0,1;0rad)
  BaseFeature = -> Fillet029
  Height = 3
  MapMode = 7
  Placement = pos=(1.5,34,4) rot=(0.57735,-0.57735,-0.57735;2.0944rad)
  Radius = 1
  Refine = true
  Support = -> [Fillet029]
  expr: Height = <<pullerBody>>.Length
  expr: .AttachmentOffset.Base.z = -Height
FEATURE [PartDesign::Body] Body009  label="triggerPuller"
  Group = -> [Box030,Wedge013,Box033,Cylinder049,Fillet028,Fillet029,Cylinder050]
  Origin = -> Origin009
  Placement = pos=(0,0,-23) rot=(0,0,1;3.14159rad)
  Tip = -> Cylinder050
FEATURE [PartDesign::AdditiveBox] Box034
  AttacherType = Attacher::AttachEngine3D
  AttachmentOffset = pos=(-0.5,-18.75,42) rot=(0,0,1;0rad)
  BaseFeature = -> Box031
  Height = 3
  Length = 1
  MapMode = 5
  Placement = pos=(-0.5,-42,-18.75) rot=(1,0,0;1.5708rad)
  Refine = true
  Support = -> [XZ_Plane008]
  Width = 5
  expr: .AttachmentOffset.Base.y = -<<air_chamber>>.Radius - Width
  expr: .AttachmentOffset.Base.x = -Length / 2
  expr: .AttachmentOffset.Base.z = <<pullerBody>>.Width + <<Box033>>.Width - <<cap_body>>.Height + 1mm
  expr: Width = Sketch.Constraints.wallThickness + 3mm
FEATURE [PartDesign::Body] Body008  label="bodyWithSightWithTriggerFrame"
  Group = -> [Cylinder042,Box027,Sphere013,Sphere014,Cylinder048,Cylinder045,Cylinder040,Cylinder044,Sphere012,Cylinder043,Sphere011,Cylinder047,PolarPattern006,Cylinder046,PolarPattern007,Box028,Mirrored015,Cylinder041,Mirrored016,Fillet026,Fillet027,Wedge010,Wedge009,Wedge011,Box029,Box031,Box034]
  Origin = -> Origin008
  Tip = -> Box034
FEATURE [PartDesign::Chamfer] Chamfer
  Angle = 45
  Base = -> Mirrored [Edge24]
  BaseFeature = -> Mirrored
  ChamferType = 0
  FlipDirection = false
  Placement = pos=(8,4e-15,-16.25) rot=(1,0,0;1.5708rad)
  Refine = true
  Size = 2
  Size2 = 1
  SupportTransform = false
FEATURE [PartDesign::Body] Body002  label="trigger"
  Group = -> [Cylinder013,Box007,Cylinder011,Cylinder012,Cylinder014,Box005,Wedge001,Box006,Mirrored,Chamfer]
  Origin = -> Origin002
  Placement = pos=(0,6,0) rot=(0,0,1;3.14159rad)
  Tip = -> Chamfer
